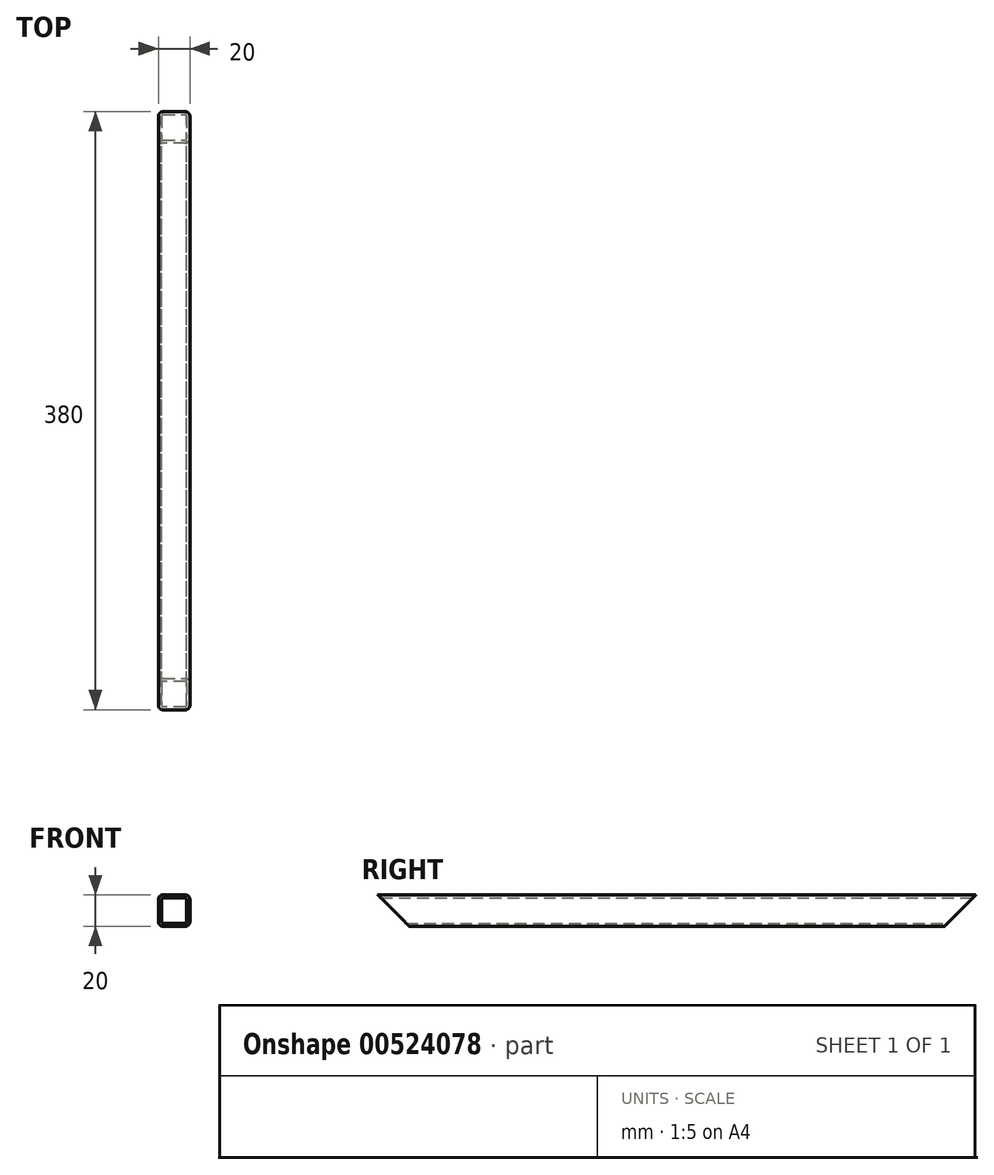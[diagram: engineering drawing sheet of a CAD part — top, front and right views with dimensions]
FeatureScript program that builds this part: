
annotation { "Feature Type Name" : "Feature", "Feature Type Description" : "" }
export const myFeature = defineFeature(function(context is Context, id is Id, definition is map)
    precondition{}
    {
        {
            assignVariable(context, id + "F0", {"name" : "R", "anyValue" : 3});
        }
        {
            assignVariable(context, id + "F1", {"name" : "W", "anyValue" : 2});
        }
        {
            var Q0;
            Q0=qCreatedBy(makeId("Front.planeOp"),FACE);
            var sketch = newSketch(context, id + "F2", { "sketchPlane" : qUnion([Q0])});
            skLineSegment(sketch, "E0.bottom", {"start": v(-10, 10) * mm, "end": v(10, 10) * mm});
            skLineSegment(sketch, "E0.top", {"start": v(-10, -10) * mm, "end": v(10, -10) * mm});
            skLineSegment(sketch, "E0.left", {"start": v(-10, 10) * mm, "end": v(-10, -10) * mm});
            skLineSegment(sketch, "E0.right", {"start": v(10, 10) * mm, "end": v(10, -10) * mm});
            skSolve(sketch);
        }
        {
            var Q0;
            Q0=qSketchRegion(id+"F2",true);
            extrude(context, id + "F3", {"entities" : qUnion([Q0]), "endBound" : BoundingType.SYMMETRIC, "depth" : 380 * mm, "offsetDistance" : 25 * mm});
        }
        {
            var Q0;
            Q0=makeQuery(id+"F3.opExtrude","SWEPT_EDGE",EDGE,{"disambiguationData":[OSD([sQuery(id+"F2.wireOp",EDGE,"E0.bottom"),sQuery(id+"F2.wireOp",EDGE,"E0.right")])]});
            var Q1;
            Q1=makeQuery(id+"F3.opExtrude","SWEPT_EDGE",EDGE,{"disambiguationData":[OSD([sQuery(id+"F2.wireOp",EDGE,"E0.bottom"),sQuery(id+"F2.wireOp",EDGE,"E0.left")])]});
            var Q2;
            Q2=makeQuery(id+"F3.opExtrude","SWEPT_EDGE",EDGE,{"disambiguationData":[OSD([sQuery(id+"F2.wireOp",EDGE,"E0.top"),sQuery(id+"F2.wireOp",EDGE,"E0.right")])]});
            var Q3;
            Q3=makeQuery(id+"F3.opExtrude","SWEPT_EDGE",EDGE,{"disambiguationData":[OSD([sQuery(id+"F2.wireOp",EDGE,"E0.top"),sQuery(id+"F2.wireOp",EDGE,"E0.left")])]});
            fillet(context, id + "F4", {"entities" : qUnion([Q0, Q1, Q2, Q3]), "radius" : (getVariable(context, 'R')) * mm, "tangentPropagation" : true, "allowEdgeOverflow" : false});
        }
        {
            var Q0;
            Q0=makeQuery(id+"F3.opExtrude","CAP_FACE",FACE,{"disambiguationData":[OSD([sQuery(id+"F2.wireOp",EDGE,"E0.bottom"),sQuery(id+"F2.wireOp",EDGE,"E0.top"),sQuery(id+"F2.wireOp",EDGE,"E0.left"),sQuery(id+"F2.wireOp",EDGE,"E0.right")])],"isStart":false});
            var Q1;
            Q1=makeQuery(id+"F3.opExtrude","CAP_FACE",FACE,{"disambiguationData":[OSD([sQuery(id+"F2.wireOp",EDGE,"E0.bottom"),sQuery(id+"F2.wireOp",EDGE,"E0.top"),sQuery(id+"F2.wireOp",EDGE,"E0.left"),sQuery(id+"F2.wireOp",EDGE,"E0.right")])],"isStart":true});
            shell(context, id + "F5", {"entities" : qUnion([Q0, Q1]), "thickness" : (getVariable(context, 'W')) * mm});
        }
        {
            var Q0;
            Q0=makeQuery(id+"F3.opExtrude","SWEPT_FACE",FACE,{"disambiguationData":[OSD([sQuery(id+"F2.wireOp",EDGE,"E0.left")])]});
            var sketch = newSketch(context, id + "F6", { "sketchPlane" : qUnion([Q0])});
            skLineSegment(sketch, "E1", {"start": v(-190, -10) * mm, "end": v(-170, -10) * mm});
            skLineSegment(sketch, "E2", {"start": v(-170, -10) * mm, "end": v(-190, 10) * mm});
            skLineSegment(sketch, "E3", {"start": v(-190, 10) * mm, "end": v(-190, -10) * mm});
            skSolve(sketch);
        }
        {
            var Q0;
            Q0=qSketchRegion(id+"F6",true);
            extrude(context, id + "F7", {"entities" : qUnion([Q0]), "operationType" : NewBodyOperationType.REMOVE, "endBound" : BoundingType.THROUGH_ALL, "oppositeDirection" : true, "depth" : 25 * mm, "offsetDistance" : 25 * mm});
        }
        {
            var Q0;
            Q0=makeQuery(id+"F3.opExtrude","SWEPT_FACE",FACE,{"disambiguationData":[OSD([sQuery(id+"F2.wireOp",EDGE,"E0.right")])]});
            var sketch = newSketch(context, id + "F8", { "sketchPlane" : qUnion([Q0])});
            skLineSegment(sketch, "E4.0", {"start": v(170, -10) * mm, "end": v(-190, -10) * mm, "construction": true});
            skLineSegment(sketch, "E4.1", {"start": v(-190, 10) * mm, "end": v(190, 10) * mm, "construction": true});
            skLineSegment(sketch, "E5", {"start": v(-170, -10) * mm, "end": v(-190, 10) * mm});
            skLineSegment(sketch, "E6", {"start": v(-190, -10) * mm, "end": v(-170, -10) * mm});
            skLineSegment(sketch, "E7", {"start": v(-190, 10) * mm, "end": v(-190, -10) * mm});
            skSolve(sketch);
        }
        {
            var Q0;
            Q0=qSketchRegion(id+"F8",true);
            extrude(context, id + "F9", {"entities" : qUnion([Q0]), "operationType" : NewBodyOperationType.REMOVE, "endBound" : BoundingType.THROUGH_ALL, "oppositeDirection" : true, "depth" : 25 * mm, "offsetDistance" : 25 * mm});
        }
    });
